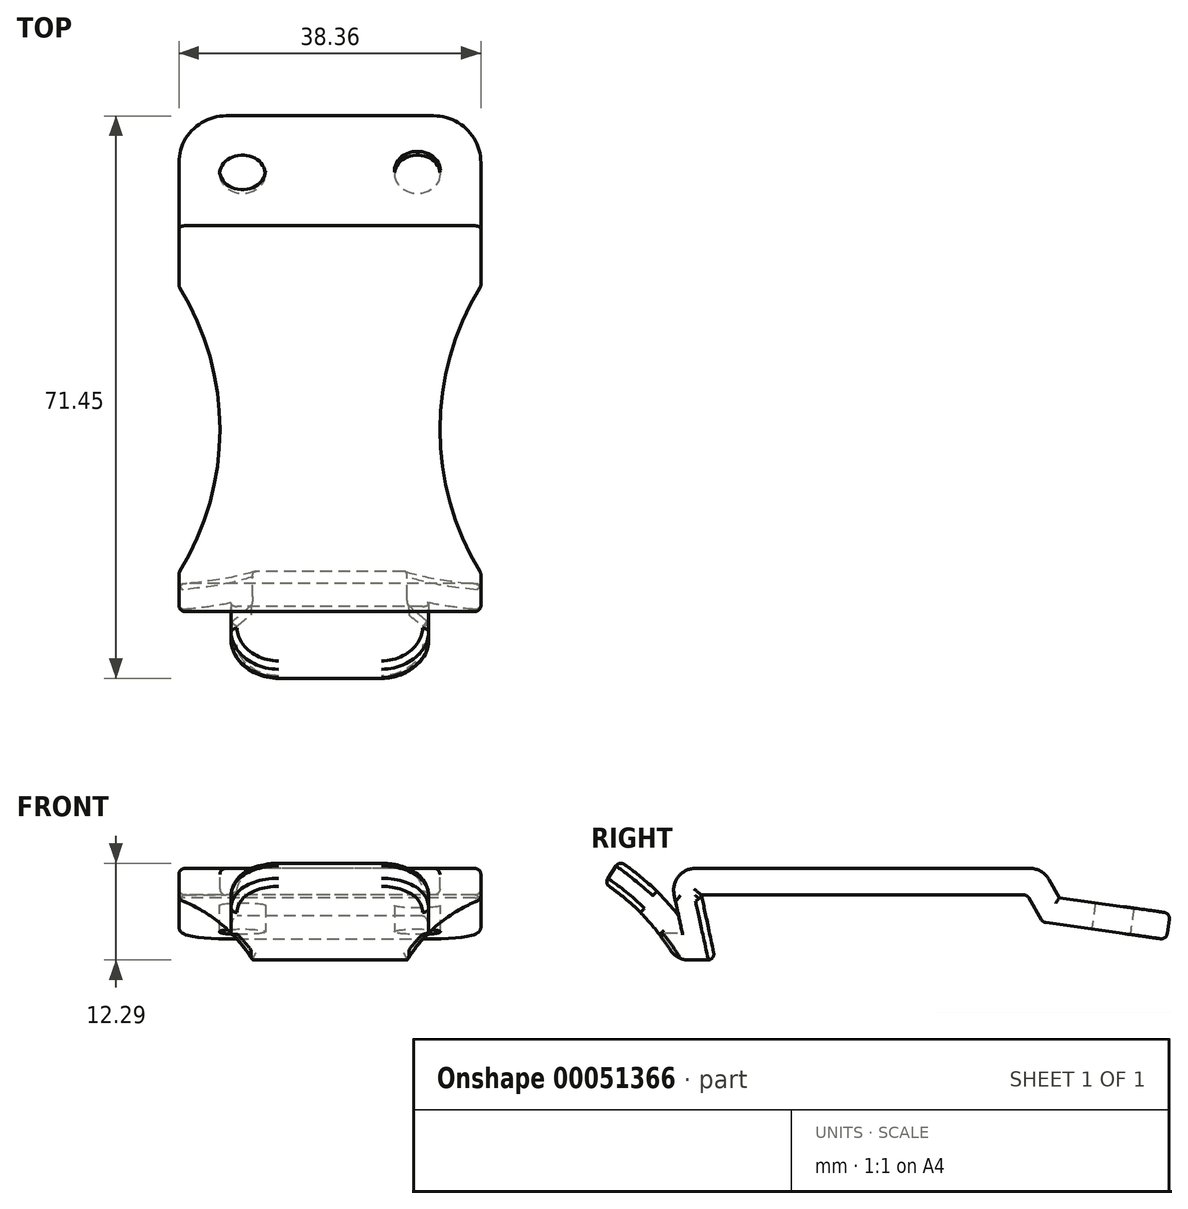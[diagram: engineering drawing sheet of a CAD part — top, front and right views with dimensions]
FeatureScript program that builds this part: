
annotation { "Feature Type Name" : "Feature", "Feature Type Description" : "" }
export const myFeature = defineFeature(function(context is Context, id is Id, definition is map)
    precondition{}
    {
        {
            var Q0;
            Q0=qCreatedBy(makeId("Right.planeOp"),FACE);
            var sketch = newSketch(context, id + "F0", { "sketchPlane" : qUnion([Q0])});
            skLineSegment(sketch, "E0", {"start": v(-17.48, 0) * mm, "end": v(23.9, 0) * mm});
            skLineSegment(sketch, "E1", {"start": v(23.9, 0) * mm, "end": v(25.9, -3.45) * mm});
            skLineSegment(sketch, "E2", {"start": v(25.9, -3.45) * mm, "end": v(41.6, -5.66) * mm});
            skLineSegment(sketch, "E3", {"start": v(-17.48, 0) * mm, "end": v(-15.72, -8.26) * mm});
            skLineSegment(sketch, "E4", {"start": v(-15.72, -8.26) * mm, "end": v(-20.67, -8.26) * mm});
            skLineSegment(sketch, "E5", {"start": v(-20.67, -8.26) * mm, "end": v(-29.78, 1.51) * mm, "construction": true});
            skArc(sketch, "E6", {"start": v(-20.67, -8.26) * mm, "mid": v(-24.65, -2.83) * mm, "end": v(-29.78, 1.51) * mm});
            skLineSegment(sketch, "E7.0", {"start": v(28, -0.34) * mm, "end": v(42.06, -2.31) * mm});
            skLineSegment(sketch, "E7.1", {"start": v(25.85, 3.38) * mm, "end": v(28, -0.34) * mm});
            skLineSegment(sketch, "E7.2", {"start": v(-21.65, 3.38) * mm, "end": v(25.85, 3.38) * mm});
            skArc(sketch, "E8.0", {"start": v(-20.37, -2.65) * mm, "mid": v(-23.86, 1.15) * mm, "end": v(-27.92, 4.33) * mm});
            skLineSegment(sketch, "E9", {"start": v(-20.37, -2.65) * mm, "end": v(-21.65, 3.38) * mm});
            skLineSegment(sketch, "E10", {"start": v(-27.92, 4.33) * mm, "end": v(-29.78, 1.51) * mm});
            skLineSegment(sketch, "E11", {"start": v(42.06, -2.31) * mm, "end": v(41.6, -5.66) * mm});
            skPoint(sketch, "E12", {"position": v(2.1, 3.38) * mm});
            skLineSegment(sketch, "E13", {"start": v(-20.37, -2.65) * mm, "end": v(-19.17, -8.26) * mm});
            skSolve(sketch);
        }
        {
            var Q0;
            Q0=makeQuery(id+"F0.imprint","IMPRINT",FACE,{"disambiguationData":[TD([[makeQuery(id+"F0.imprint","IMPRINT",EDGE,{"derivedFrom":sQuery(id+"F0.wireOp",EDGE,"E0")}),1.0]])]});
            extrude(context, id + "F1", {"entities" : qUnion([Q0]), "endBound" : BoundingType.SYMMETRIC, "depth" : 38.35 * mm});
        }
        {
            var Q0;
            {var subQ0=sQuery(id+"F0.wireOp",EDGE,"E6");Q0=makeQuery(id+"F0.imprint","IMPRINT",FACE,{"disambiguationData":[TD([[makeQuery(id+"F0.imprint","IMPRINT",EDGE,{"derivedFrom":subQ0}),-1.0]])]});}
            extrude(context, id + "F2", {"entities" : qUnion([Q0]), "operationType" : NewBodyOperationType.ADD, "endBound" : BoundingType.SYMMETRIC, "depth" : 25.07 * mm});
        }
        {
            var Q0;
            Q0=makeQuery(id+"F1.opExtrude","SWEPT_FACE",FACE,{"disambiguationData":[OSD([sQuery(id+"F0.wireOp",EDGE,"E7.2")])]});
            var sketch = newSketch(context, id + "F3", { "sketchPlane" : qUnion([Q0])});
            skArc(sketch, "E14", {"start": v(19.18, 20.32) * mm, "mid": v(13.97, 2.1) * mm, "end": v(19.18, -16.1) * mm});
            skLineSegment(sketch, "E15", {"start": v(19.18, 20.32) * mm, "end": v(19.18, -16.1) * mm});
            skPoint(sketch, "E16", {"position": v(19.18, 2.1) * mm});
            skArc(sketch, "E17.MirrorCS", {"start": v(-19.18, 20.32) * mm, "mid": v(-13.97, 2.1) * mm, "end": v(-19.18, -16.1) * mm});
            skLineSegment(sketch, "E18.MirrorCS", {"start": v(-19.18, 20.32) * mm, "end": v(-19.18, -16.1) * mm});
            skSolve(sketch);
        }
        {
            var Q0;
            Q0 = qSketchRegion(id + "F3", true);
            extrude(context, id + "F4", {"entities" : qUnion([Q0]), "operationType" : NewBodyOperationType.REMOVE, "endBound" : BoundingType.THROUGH_ALL, "oppositeDirection" : true, "depth" : 25.4 * mm});
        }
        {
            var Q0;
            Q0=qCreatedBy(makeId("Front.planeOp"),FACE);
            var sketch = newSketch(context, id + "F5", { "sketchPlane" : qUnion([Q0])});
            skArc(sketch, "E19", {"start": v(19.18, -0.58) * mm, "mid": v(13.86, -3.65) * mm, "end": v(9.8, -8.26) * mm});
            skLineSegment(sketch, "E20", {"start": v(19.18, -0.58) * mm, "end": v(19.18, -8.26) * mm});
            skLineSegment(sketch, "E21", {"start": v(19.18, -8.26) * mm, "end": v(9.8, -8.26) * mm});
            skArc(sketch, "E22.MirrorCS", {"start": v(-19.18, -0.58) * mm, "mid": v(-13.86, -3.65) * mm, "end": v(-9.8, -8.26) * mm});
            skLineSegment(sketch, "E23.MirrorCS", {"start": v(-19.18, -8.26) * mm, "end": v(-9.8, -8.26) * mm});
            skLineSegment(sketch, "E24.MirrorCS", {"start": v(-19.18, -0.58) * mm, "end": v(-19.18, -8.26) * mm});
            skLineSegment(sketch, "E25", {"start": v(19.18, -0.58) * mm, "end": v(9.8, -8.26) * mm, "construction": true});
            skSolve(sketch);
        }
        {
            var Q0;
            Q0 = qSketchRegion(id + "F5", true);
            extrude(context, id + "F6", {"entities" : qUnion([Q0]), "operationType" : NewBodyOperationType.REMOVE, "endBound" : BoundingType.THROUGH_ALL, "depth" : 50.8 * mm});
        }
        {
            var Q0;
            Q0=makeQuery(id+"F1.opExtrude","SWEPT_FACE",FACE,{"disambiguationData":[OSD([sQuery(id+"F0.wireOp",EDGE,"E7.0")])]});
            var sketch = newSketch(context, id + "F7", { "sketchPlane" : qUnion([Q0])});
            skEllipse(sketch, "E26", {"center": v(11.11, 34.86) * mm, "majorRadius": 2.92 * mm, "minorRadius": 2.46 * mm, "majorAxis": v(1, 0)});
            skEllipse(sketch, "E27.MirrorC", {"center": v(-11.11, 34.86) * mm, "majorRadius": 2.92 * mm, "minorRadius": 2.46 * mm, "majorAxis": v(-1, 0)});
            skSolve(sketch);
        }
        {
            var Q0;
            Q0 = qSketchRegion(id + "F7", true);
            extrude(context, id + "F8", {"entities" : qUnion([Q0]), "operationType" : NewBodyOperationType.REMOVE, "oppositeDirection" : true, "depth" : 25.4 * mm});
        }
        {
            var Q0;
            Q0=makeQuery(id+"F1.opExtrude","CAP_EDGE",EDGE,{"disambiguationData":[OSD([sQuery(id+"F0.wireOp",EDGE,"E11")])],"isStart":false});
            var Q1;
            Q1=makeQuery(id+"F1.opExtrude","CAP_EDGE",EDGE,{"disambiguationData":[OSD([sQuery(id+"F0.wireOp",EDGE,"E11")])],"isStart":true});
            var Q2;
            Q2=makeQuery(id+"F2.opExtrude","CAP_EDGE",EDGE,{"disambiguationData":[OSD([sQuery(id+"F0.wireOp",EDGE,"E10")])],"isStart":false});
            var Q3;
            Q3=makeQuery(id+"F2.opExtrude","CAP_EDGE",EDGE,{"disambiguationData":[OSD([sQuery(id+"F0.wireOp",EDGE,"E10")])],"isStart":true});
            fillet(context, id + "F9", {"entities" : qUnion([Q0, Q1, Q2, Q3]), "radius" : 6 * mm, "tangentPropagation" : true, "allowEdgeOverflow" : false});
        }
        {
            var Q0;
            Q0=makeQuery(id+"F1.opExtrude","SWEPT_EDGE",EDGE,{"disambiguationData":[OSD([sQuery(id+"F0.wireOp",EDGE,"E7.2"),sQuery(id+"F0.wireOp",EDGE,"E9")])]});
            var Q1;
            Q1=makeQuery(id+"F1.opExtrude","SWEPT_EDGE",EDGE,{"disambiguationData":[OSD([sQuery(id+"F0.wireOp",EDGE,"E7.1"),sQuery(id+"F0.wireOp",EDGE,"E7.2")])]});
            var Q2;
            Q2=makeQuery(id+"F2.opExtrude","SWEPT_EDGE",EDGE,{"disambiguationData":[OSD([sQuery(id+"F0.wireOp",EDGE,"E4"),sQuery(id+"F0.wireOp",EDGE,"E6")])]});
            fillet(context, id + "F10", {"entities" : qUnion([Q0, Q1, Q2]), "radius" : 2.75 * mm, "tangentPropagation" : true, "allowEdgeOverflow" : false});
        }
        {
            var Q0;
            Q0=makeQuery(id+"F4.boolean.opBoolean","COPY",FACE,{"disambiguationData":[OD(0.0)],"derivedFrom":makeQuery(id+"F4.opExtrude","SWEPT_FACE",FACE,{"disambiguationData":[OSD([sQuery(id+"F3.wireOp",EDGE,"E14")])]})});
            var Q1;
            {var subQ0=sQuery(id+"F0.wireOp",EDGE,"E7.2");var subQ1=sQuery(id+"F0.wireOp",EDGE,"E4");var subQ2=sQuery(id+"F0.wireOp",EDGE,"E3");var subQ3=sQuery(id+"F0.wireOp",EDGE,"E0");var subQ4=sQuery(id+"F0.wireOp",EDGE,"E13");var subQ5=sQuery(id+"F0.wireOp",EDGE,"E9");Q1=makeQuery(id+"F4.boolean.opBoolean","SPLIT",FACE,{"disambiguationData":[TD([makeQuery(id+"F1.opExtrude","SWEPT_FACE",FACE,{"disambiguationData":[OSD([subQ2])]})])],"derivedFrom":makeQuery(id+"F1.opExtrude","CAP_FACE",FACE,{"disambiguationData":[OSD([subQ3,sQuery(id+"F0.wireOp",EDGE,"E1"),sQuery(id+"F0.wireOp",EDGE,"E2"),subQ2,subQ1,sQuery(id+"F0.wireOp",EDGE,"E7.0"),sQuery(id+"F0.wireOp",EDGE,"E7.1"),subQ0,subQ5,sQuery(id+"F0.wireOp",EDGE,"E11"),subQ4])],"isStart":false})});}
            var Q2;
            {var subQ0=sQuery(id+"F0.wireOp",EDGE,"E10");Q2=makeQuery(id+"F9.opFillet","BLEND_FACE",FACE,{"disambiguationData":[OSD([subQ0]),TDD([makeQuery(id+"F2.opExtrude","CAP_EDGE",EDGE,{"disambiguationData":[OSD([subQ0])],"isStart":false})])]});}
            var Q3;
            {var subQ0=sQuery(id+"F0.wireOp",EDGE,"E7.0");var subQ1=sQuery(id+"F0.wireOp",EDGE,"E2");var subQ2=sQuery(id+"F0.wireOp",EDGE,"E1");var subQ3=sQuery(id+"F0.wireOp",EDGE,"E0");var subQ4=sQuery(id+"F0.wireOp",EDGE,"E7.1");var subQ5=sQuery(id+"F0.wireOp",EDGE,"E7.2");var subQ6=sQuery(id+"F0.wireOp",EDGE,"E11");Q3=makeQuery(id+"F4.boolean.opBoolean","SPLIT",FACE,{"disambiguationData":[TD([makeQuery(id+"F1.opExtrude","SWEPT_FACE",FACE,{"disambiguationData":[OSD([subQ2])]})])],"derivedFrom":makeQuery(id+"F1.opExtrude","CAP_FACE",FACE,{"disambiguationData":[OSD([subQ3,subQ2,subQ1,sQuery(id+"F0.wireOp",EDGE,"E3"),sQuery(id+"F0.wireOp",EDGE,"E4"),subQ0,subQ4,subQ5,sQuery(id+"F0.wireOp",EDGE,"E9"),subQ6,sQuery(id+"F0.wireOp",EDGE,"E13")])],"isStart":false})});}
            var Q4;
            Q4=makeQuery(id+"F4.boolean.opBoolean","COPY",FACE,{"disambiguationData":[OD(0.0)],"derivedFrom":makeQuery(id+"F4.opExtrude","SWEPT_FACE",FACE,{"disambiguationData":[OSD([sQuery(id+"F3.wireOp",EDGE,"E17.MirrorCS")])]})});
            var Q5;
            {var subQ0=sQuery(id+"F0.wireOp",EDGE,"E7.0");var subQ1=sQuery(id+"F0.wireOp",EDGE,"E2");var subQ2=sQuery(id+"F0.wireOp",EDGE,"E1");var subQ3=sQuery(id+"F0.wireOp",EDGE,"E0");var subQ4=sQuery(id+"F0.wireOp",EDGE,"E7.1");var subQ5=sQuery(id+"F0.wireOp",EDGE,"E7.2");var subQ6=sQuery(id+"F0.wireOp",EDGE,"E11");Q5=makeQuery(id+"F4.boolean.opBoolean","SPLIT",FACE,{"disambiguationData":[TD([makeQuery(id+"F1.opExtrude","SWEPT_FACE",FACE,{"disambiguationData":[OSD([subQ2])]})])],"derivedFrom":makeQuery(id+"F1.opExtrude","CAP_FACE",FACE,{"disambiguationData":[OSD([subQ3,subQ2,subQ1,sQuery(id+"F0.wireOp",EDGE,"E3"),sQuery(id+"F0.wireOp",EDGE,"E4"),subQ0,subQ4,subQ5,sQuery(id+"F0.wireOp",EDGE,"E9"),subQ6,sQuery(id+"F0.wireOp",EDGE,"E13")])],"isStart":true})});}
            var Q6;
            {var subQ0=sQuery(id+"F0.wireOp",EDGE,"E7.2");var subQ1=sQuery(id+"F0.wireOp",EDGE,"E4");var subQ2=sQuery(id+"F0.wireOp",EDGE,"E3");var subQ3=sQuery(id+"F0.wireOp",EDGE,"E0");var subQ4=sQuery(id+"F0.wireOp",EDGE,"E13");var subQ5=sQuery(id+"F0.wireOp",EDGE,"E9");Q6=makeQuery(id+"F4.boolean.opBoolean","SPLIT",FACE,{"disambiguationData":[TD([makeQuery(id+"F1.opExtrude","SWEPT_FACE",FACE,{"disambiguationData":[OSD([subQ2])]})])],"derivedFrom":makeQuery(id+"F1.opExtrude","CAP_FACE",FACE,{"disambiguationData":[OSD([subQ3,sQuery(id+"F0.wireOp",EDGE,"E1"),sQuery(id+"F0.wireOp",EDGE,"E2"),subQ2,subQ1,sQuery(id+"F0.wireOp",EDGE,"E7.0"),sQuery(id+"F0.wireOp",EDGE,"E7.1"),subQ0,subQ5,sQuery(id+"F0.wireOp",EDGE,"E11"),subQ4])],"isStart":true})});}
            var Q7;
            Q7=makeQuery(id+"F1.opExtrude","SWEPT_FACE",FACE,{"disambiguationData":[OSD([sQuery(id+"F0.wireOp",EDGE,"E1")])]});
            fillet(context, id + "F11", {"entities" : qUnion([Q0, Q1, Q2, Q3, Q4, Q5, Q6, Q7]), "radius" : 0.76 * mm, "tangentPropagation" : true, "allowEdgeOverflow" : false});
        }
        {
            var Q0;
            Q0=makeQuery(id+"F6.boolean.opBoolean","INTERSECT",EDGE,{"derivedFrom":[makeQuery(id+"F1.opExtrude","SWEPT_FACE",FACE,{"disambiguationData":[OSD([sQuery(id+"F0.wireOp",EDGE,"E3")])]}),makeQuery(id+"F6.opExtrude","SWEPT_FACE",FACE,{"disambiguationData":[OSD([sQuery(id+"F5.wireOp",EDGE,"E19")])]})]});
            var Q1;
            Q1=makeQuery(id+"F6.boolean.opBoolean","INTERSECT",EDGE,{"derivedFrom":[makeQuery(id+"F1.opExtrude","SWEPT_FACE",FACE,{"disambiguationData":[OSD([sQuery(id+"F0.wireOp",EDGE,"E3")])]}),makeQuery(id+"F6.opExtrude","SWEPT_FACE",FACE,{"disambiguationData":[OSD([sQuery(id+"F5.wireOp",EDGE,"E22.MirrorCS")])]})]});
            var Q2;
            Q2=makeQuery(id+"F1.opExtrude","SWEPT_EDGE",EDGE,{"disambiguationData":[OSD([sQuery(id+"F0.wireOp",EDGE,"E3"),sQuery(id+"F0.wireOp",EDGE,"E4")])]});
            var Q3;
            Q3=makeQuery(id+"F6.boolean.opBoolean","INTERSECT",EDGE,{"derivedFrom":[makeQuery(id+"F2.opExtrude","SWEPT_FACE",FACE,{"disambiguationData":[OSD([sQuery(id+"F0.wireOp",EDGE,"E6")])]}),makeQuery(id+"F6.opExtrude","SWEPT_FACE",FACE,{"disambiguationData":[OSD([sQuery(id+"F5.wireOp",EDGE,"E19")])]})]});
            var Q4;
            Q4=makeQuery(id+"F6.boolean.opBoolean","COPY",EDGE,{"derivedFrom":makeQuery(id+"F6.opExtrude","SWEPT_EDGE",EDGE,{"disambiguationData":[OSD([sQuery(id+"F5.wireOp",EDGE,"E19"),sQuery(id+"F5.wireOp",EDGE,"E21")])]})});
            var Q5;
            Q5=makeQuery(id+"F6.boolean.opBoolean","INTERSECT",EDGE,{"derivedFrom":[makeQuery(id+"F2.opExtrude","CAP_FACE",FACE,{"disambiguationData":[OSD([sQuery(id+"F0.wireOp",EDGE,"E4"),sQuery(id+"F0.wireOp",EDGE,"E6"),sQuery(id+"F0.wireOp",EDGE,"E8.0"),sQuery(id+"F0.wireOp",EDGE,"E10"),sQuery(id+"F0.wireOp",EDGE,"E13")])],"isStart":false}),makeQuery(id+"F6.opExtrude","SWEPT_FACE",FACE,{"disambiguationData":[OSD([sQuery(id+"F5.wireOp",EDGE,"E19")])]})]});
            var Q6;
            Q6=makeQuery(id+"F6.boolean.opBoolean","COPY",EDGE,{"derivedFrom":makeQuery(id+"F6.opExtrude","SWEPT_EDGE",EDGE,{"disambiguationData":[OSD([sQuery(id+"F5.wireOp",EDGE,"E22.MirrorCS"),sQuery(id+"F5.wireOp",EDGE,"E23.MirrorCS")])]})});
            var Q7;
            Q7=makeQuery(id+"F6.boolean.opBoolean","INTERSECT",EDGE,{"derivedFrom":[makeQuery(id+"F2.opExtrude","SWEPT_FACE",FACE,{"disambiguationData":[OSD([sQuery(id+"F0.wireOp",EDGE,"E6")])]}),makeQuery(id+"F6.opExtrude","SWEPT_FACE",FACE,{"disambiguationData":[OSD([sQuery(id+"F5.wireOp",EDGE,"E22.MirrorCS")])]})]});
            fillet(context, id + "F12", {"entities" : qUnion([Q0, Q1, Q2, Q3, Q4, Q5, Q6, Q7]), "radius" : 0.76 * mm, "allowEdgeOverflow" : false});
        }
    });
